# Revit family: Reggiani EVO Ø 60mm  Performance
name_source: partatom
category: Modelli generici
revit_build: Autodesk Revit 2016 (Build: 20150220_1215(x64)
units: mm (PartAtom-declared; Revit-internal decimal feet)

## family parameters
Condiviso = No
Host = Superficie
Punto di calcolo locali = No
Può ospitare armatura = No
Quota connettore circolare = Usa diametro
Taglio con vuoti quando caricato = No
Tipo di parte = Normale

## types (3) — shared parameters
Brand url = http://www.reggiani.net
Design country = Italy
Edition number = 1
Installation instructions = http://www.reggiani.net
Manufacturer country = Italy
Manufacturer name = Reggiani
Material main = Aluminium
Nominal height = 117 mm  [stored 0.383858 ft]
Nominal width = 60 mm  [stored 0.19685 ft]
Product Guid = bc5f8e87-a0cc-467e-9572-0e7587368257
Product SKU = yori_evo_box_60
Product certification = http://www.reggiani.net
Product data url = https://bimobject.com
Product family = Track fixture
Product group = Yori
Product url = http://www.reggiani.net
Produttore = Reggiani Spa Illuminazione
Viale Monza 16, 
20845 Sovico (MB) Italia
Prospetto di default = 1219 mm
QR code = http://bimobject.com
Rotation oriz = 90.00°
Technical description = http://www.reggiani.net Brochure_Mains Voltage (10).pdf
URL = http://www.reggiani.net
Weight Net (Kg) = 0.65
body = Reggiani Alluminio  white

## per-type parameters (varying)
| type | Modello |
| Reggiani EVO  Ø 60mm  Performance- mod GH92  K- B- E-H | Reggiani EVO  Ø 60mm  Performance- mod GH92  K- B- E-H |
| Reggiani EVO  Ø 60mm  Performance- mod GH 93  K- B- E-H | Reggiani EVO  Ø 60mm  Performance- mod GH93  K- B- E-H |
| Reggiani EVO  Ø 60mm  Performance- mod GH 94  K- B- E-H | Reggiani EVO  Ø 60mm  Performance- mod GH94 K- B- E-H |

note: [stored X ft] marks values corroborated as IEEE doubles in the binary element streams (Revit-internal decimal feet)
